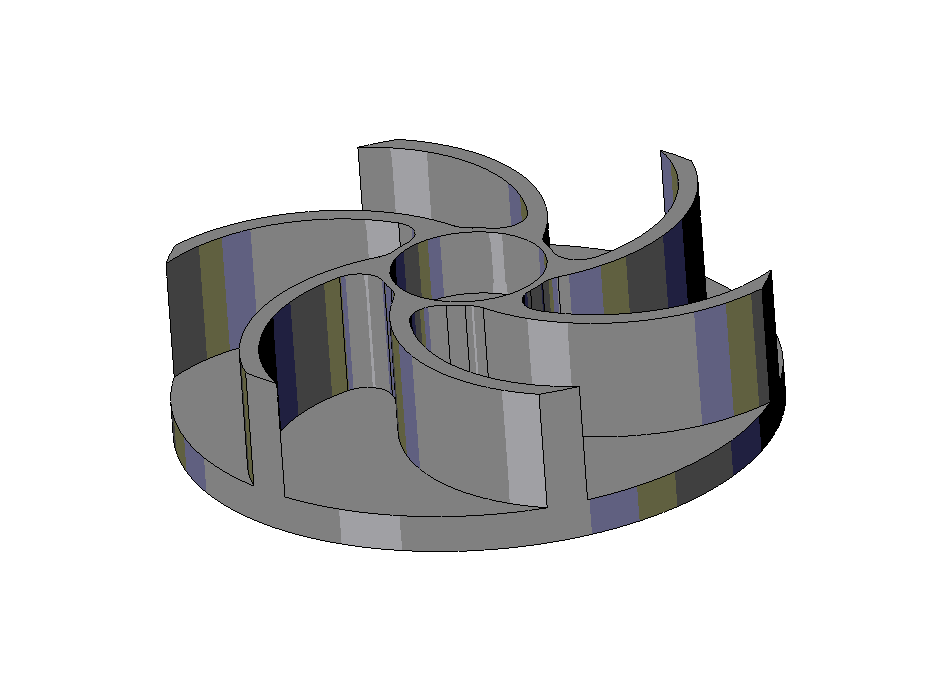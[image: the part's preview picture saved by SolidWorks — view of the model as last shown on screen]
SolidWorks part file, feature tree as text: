
SOLIDWORKS PART (.sldprt)
format: sldprt  version: not decoded by parser v0  size: 378,368 bytes
history: native  units: mm
features: sketch x7, extrude x5, pattern_circular x2, material x1, hole x1 (+12 scaffold rows collapsed)
feature tree (28):
  scaffold x12  (default folders/planes/origin — collapsed)
  material  "Material <not specified>"
  sketch  "Sketch1"  dims[D1=63.0mm]
  extrude  "Extrude1"  Depth=4mm
  sketch  "Sketch2"  dims[c1.D1=18.0mm c1.D2=70.0mm c1.D3=40.0mm c1.D4=20.0mm c2.D3=20.0mm c2.D2=19.0mm c3.D3=21.0mm c3.D4=20.0mm c3.D5=~28.160342mm c3.D6=20.0mm c3.D7=20.0mm c3.D2=3.0mm c3.D1=9.0mm c4.D3=11.0mm c4.D1=18.0mm c4.D4=5.5mm c5.D3=3.0mm c5.D4=12.0mm c5.D5=12.0mm c5.D6=8.0mm c6.D5=35.0mm c6.D2=2.0mm c6.D3=40.0mm c7.D5=~20.295395mm c8.D5=35.0deg c8.D4=3.5mm c8.D3=~4.075917mm c8.D2=1.0mm c9.D3=1.0mm c9.D7=1.0mm c9.D8=1.0mm]
  sketch  "Sketch3"  dims[D1=18.0mm]
  extrude  "Extrude2"  Depth=10mm
  hole  "M11.0 (11) Diameter Hole1"  Diameter=11mm Depth=10mm
  sketch  "Sketch5"
  sketch  "Sketch4"  dims[hole-wizard template sketch: 47 standard entries collapsed; hole parameters kept: c15.Hole Depth=10.0mm c15.D3=~14.816244mm c15.Drill Angle=118.0deg]
  extrude  "Extrude3"  Depth=13mm
  pattern_circular  "CirPattern1"  Count=4 Angle=360deg
  extrude  "Extrude4"  [1 undecoded]
  sketch  "Sketch2<8>"  dims[D1=13.0mm]
  pattern_circular  "CirPattern2"  Count=6 Angle=360deg
  sketch  "Sketch7"  dims[D1=16.2mm D2=18.0mm]
  extrude  "Extrude5"  [1 undecoded]
decode coverage: 12 of 15 modeling features carry decoded parameters
note: ~ marks probable driven/reference dimensions
note: 2 parameter values undecoded
note: suppression state not decoded; provenance and decode notes live in map.json
